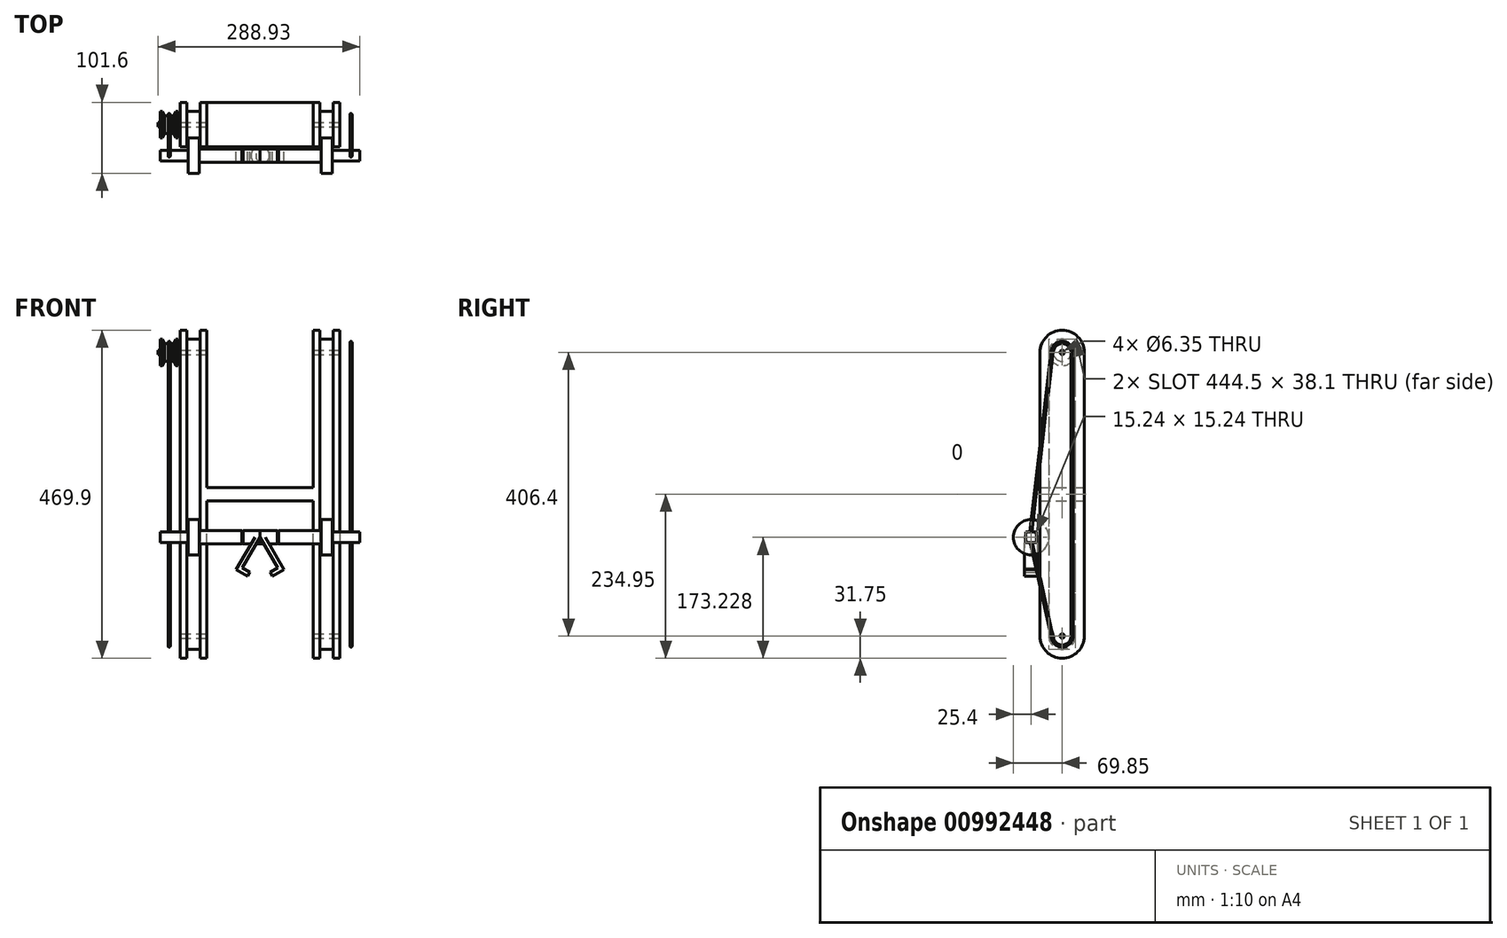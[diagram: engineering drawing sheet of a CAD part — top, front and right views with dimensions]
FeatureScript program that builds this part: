
annotation { "Feature Type Name" : "Feature", "Feature Type Description" : "" }
export const myFeature = defineFeature(function(context is Context, id is Id, definition is map)
    precondition{}
    {
        {
            var Q0;
            Q0=qCreatedBy(makeId("Front.planeOp"),FACE);
            var sketch = newSketch(context, id + "F0", { "sketchPlane" : qUnion([Q0])});
            skLineSegment(sketch, "E0", {"start": v(0, -9.53) * mm, "end": v(0, 9.53) * mm});
            skLineSegment(sketch, "E1", {"start": v(0, 9.53) * mm, "end": v(-76.2, 9.52) * mm});
            skLineSegment(sketch, "E2", {"start": v(-76.2, 9.53) * mm, "end": v(-76.2, 203.2) * mm});
            skLineSegment(sketch, "E3", {"start": v(-76.2, 203.2) * mm, "end": v(-114.3, 203.2) * mm});
            skLineSegment(sketch, "E4", {"start": v(-114.3, 203.2) * mm, "end": v(-114.3, -203.2) * mm});
            skLineSegment(sketch, "E5", {"start": v(-114.3, -203.2) * mm, "end": v(-76.2, -203.2) * mm});
            skLineSegment(sketch, "E6", {"start": v(-76.2, -203.2) * mm, "end": v(-76.2, -9.53) * mm});
            skLineSegment(sketch, "E7", {"start": v(-76.2, -9.53) * mm, "end": v(0, -9.53) * mm});
            skSolve(sketch);
        }
        {
            var Q0;
            Q0=makeQuery(id+"F0.imprint","IMPRINT",FACE,{"disambiguationData":[TD([[makeQuery(id+"F0.imprint","IMPRINT",EDGE,{"derivedFrom":sQuery(id+"F0.wireOp",EDGE,"E0")}),1.0]])]});
            extrude(context, id + "F1", {"entities" : qUnion([Q0]), "endBound" : BoundingType.SYMMETRIC, "depth" : 63.5 * mm, "offsetDistance" : 25.4 * mm});
        }
        {
            var Q0;
            Q0=makeQuery(id+"F1.opExtrude","SWEPT_FACE",FACE,{"disambiguationData":[OSD([sQuery(id+"F0.wireOp",EDGE,"E4")])]});
            var sketch = newSketch(context, id + "F2", { "sketchPlane" : qUnion([Q0])});
            skCircle(sketch, "E8", {"center": v(0, 203.2) * mm, "radius": 31.75 * mm});
            skCircle(sketch, "E9", {"center": v(0, -203.2) * mm, "radius": 31.75 * mm});
            skSolve(sketch);
        }
        {
            var Q0;
            Q0 = qSketchRegion(id + "F2", true);
            var Q1;
            Q1=makeQuery(id+"F1.opExtrude","SWEPT_FACE",FACE,{"disambiguationData":[OSD([sQuery(id+"F0.wireOp",EDGE,"E2")])]});
            extrude(context, id + "F3", {"entities" : qUnion([Q0]), "operationType" : NewBodyOperationType.ADD, "endBound" : BoundingType.UP_TO_SURFACE, "oppositeDirection" : true, "depth" : 25.4 * mm, "endBoundEntityFace" : qUnion([Q1]), "offsetDistance" : 25.4 * mm});
        }
        {
            var Q0;
            Q0=qCreatedBy(makeId("Front.planeOp"),FACE);
            var sketch = newSketch(context, id + "F4", { "sketchPlane" : qUnion([Q0])});
            skLineSegment(sketch, "E10", {"start": v(-114.3, 234.95) * mm, "end": v(-76.2, 234.95) * mm, "construction": true});
            skLineSegment(sketch, "E11.0", {"start": v(-76.2, 203.2) * mm, "end": v(-114.3, 203.2) * mm, "construction": true});
            skLineSegment(sketch, "E12.0", {"start": v(-114.3, 203.2) * mm, "end": v(-114.3, 234.95) * mm, "construction": true});
            skLineSegment(sketch, "E13.0", {"start": v(-76.2, 203.2) * mm, "end": v(-76.2, 234.95) * mm, "construction": true});
            skLineSegment(sketch, "E14", {"start": v(-114.3, 234.95) * mm, "end": v(-104.77, 234.95) * mm, "construction": true});
            skLineSegment(sketch, "E15", {"start": v(-104.77, 234.95) * mm, "end": v(-104.77, 222.25) * mm});
            skLineSegment(sketch, "E16", {"start": v(-104.77, 222.25) * mm, "end": v(-85.72, 222.25) * mm});
            skLineSegment(sketch, "E17", {"start": v(-85.72, 222.25) * mm, "end": v(-85.72, 234.95) * mm});
            skLineSegment(sketch, "E18", {"start": v(-85.72, 234.95) * mm, "end": v(-76.2, 234.95) * mm, "construction": true});
            skLineSegment(sketch, "E19", {"start": v(-104.77, 234.95) * mm, "end": v(-85.72, 234.95) * mm});
            skSolve(sketch);
        }
        {
            var Q0;
            Q0 = qSketchRegion(id + "F4", true);
            var Q1;
            Q1=makeQuery(id+"F3.opExtrude","CAP_EDGE",EDGE,{"disambiguationData":[OSD([sQuery(id+"F2.wireOp",EDGE,"E8")])],"isStart":true});
            var Q2;
            Q2=makeQuery(id+"F1.opExtrude","CAP_EDGE",EDGE,{"disambiguationData":[OSD([sQuery(id+"F0.wireOp",EDGE,"E4")])],"isStart":false});
            var Q3;
            Q3=makeQuery(id+"F1.opExtrude","CAP_EDGE",EDGE,{"disambiguationData":[OSD([sQuery(id+"F0.wireOp",EDGE,"E4")])],"isStart":true});
            var Q4;
            Q4=makeQuery(id+"F3.opExtrude","CAP_EDGE",EDGE,{"disambiguationData":[OSD([sQuery(id+"F2.wireOp",EDGE,"E9")])],"isStart":true});
            sweep(context, id + "F5", {"operationType" : NewBodyOperationType.REMOVE, "profiles" : qUnion([Q0]), "path" : qUnion([Q1, Q2, Q3, Q4])});
        }
        {
            var Q0;
            Q0=makeQuery(id+"F1.opExtrude","SWEPT_BODY",BODY,{"disambiguationData":[OSD([sQuery(id+"F0.wireOp",EDGE,"E0"),sQuery(id+"F0.wireOp",EDGE,"E1"),sQuery(id+"F0.wireOp",EDGE,"E2"),sQuery(id+"F0.wireOp",EDGE,"E3"),sQuery(id+"F0.wireOp",EDGE,"E4"),sQuery(id+"F0.wireOp",EDGE,"E5"),sQuery(id+"F0.wireOp",EDGE,"E6"),sQuery(id+"F0.wireOp",EDGE,"E7")])]});
            var Q1;
            Q1=qCreatedBy(makeId("Right.planeOp"),FACE);
            mirror(context, id + "F6", {"operationType" : NewBodyOperationType.ADD, "entities" : qUnion([Q0]), "mirrorPlane" : qUnion([Q1])});
        }
        {
            var Q0;
            Q0=makeQuery(id+"F6.opPattern","COPY",FACE,{"derivedFrom":makeQuery(id+"F3.boolean.opBoolean","MERGE",FACE,{"derivedFrom":[makeQuery(id+"F1.opExtrude","SWEPT_FACE",FACE,{"disambiguationData":[OSD([sQuery(id+"F0.wireOp",EDGE,"E4")])]}),makeQuery(id+"F3.opExtrude","CAP_FACE",FACE,{"disambiguationData":[OSD([sQuery(id+"F2.wireOp",EDGE,"E8")])],"isStart":true}),makeQuery(id+"F3.opExtrude","CAP_FACE",FACE,{"disambiguationData":[OSD([sQuery(id+"F2.wireOp",EDGE,"E9")])],"isStart":true})]}),"instanceName":"1"});
            var sketch = newSketch(context, id + "F7", { "sketchPlane" : qUnion([Q0])});
            skArc(sketch, "E20.0", {"start": v(-31.75, 203.2) * mm, "mid": v(0, 234.95) * mm, "end": v(31.75, 203.2) * mm, "construction": true});
            skCircle(sketch, "E21", {"center": v(0, 203.2) * mm, "radius": 3.18 * mm});
            skCircle(sketch, "E22.MirrorC", {"center": v(0, -203.2) * mm, "radius": 3.18 * mm});
            skSolve(sketch);
        }
        {
            var Q0;
            Q0 = qSketchRegion(id + "F7", true);
            extrude(context, id + "F8", {"entities" : qUnion([Q0]), "operationType" : NewBodyOperationType.REMOVE, "endBound" : BoundingType.THROUGH_ALL, "oppositeDirection" : true, "depth" : 25.4 * mm, "offsetDistance" : 25.4 * mm});
        }
        {
            var Q0;
            Q0=qCreatedBy(makeId("Front.planeOp"),FACE);
            var sketch = newSketch(context, id + "F9", { "sketchPlane" : qUnion([Q0])});
            skLineSegment(sketch, "E23.0", {"start": v(-104.77, 203.2) * mm, "end": v(-114.3, 203.2) * mm});
            skLineSegment(sketch, "E24.0", {"start": v(-114.3, 203.2) * mm, "end": v(-114.3, 234.95) * mm, "construction": true});
            skLineSegment(sketch, "E25", {"start": v(-114.3, 203.2) * mm, "end": v(-146.05, 203.2) * mm});
            skLineSegment(sketch, "E26", {"start": v(-146.05, 203.2) * mm, "end": v(-146.05, 206.38) * mm});
            skLineSegment(sketch, "E27", {"start": v(-146.05, 206.38) * mm, "end": v(-142.87, 206.38) * mm});
            skLineSegment(sketch, "E28", {"start": v(-142.87, 206.38) * mm, "end": v(-142.87, 222.25) * mm});
            skLineSegment(sketch, "E29", {"start": v(-142.87, 222.25) * mm, "end": v(-139.7, 222.25) * mm});
            skLineSegment(sketch, "E30", {"start": v(-139.7, 222.25) * mm, "end": v(-136.52, 215.9) * mm});
            skLineSegment(sketch, "E31", {"start": v(-136.52, 215.9) * mm, "end": v(-123.82, 215.9) * mm});
            skLineSegment(sketch, "E32", {"start": v(-123.82, 215.9) * mm, "end": v(-120.65, 222.25) * mm});
            skLineSegment(sketch, "E33", {"start": v(-120.65, 222.25) * mm, "end": v(-117.47, 222.25) * mm});
            skLineSegment(sketch, "E34", {"start": v(-117.47, 222.25) * mm, "end": v(-117.47, 206.38) * mm});
            skLineSegment(sketch, "E35", {"start": v(-117.47, 206.38) * mm, "end": v(-114.3, 206.38) * mm});
            skLineSegment(sketch, "E36", {"start": v(-114.3, 206.38) * mm, "end": v(-114.3, 203.2) * mm});
            skCircle(sketch, "E37", {"center": v(-130.17, 217.49) * mm, "radius": 1.59 * mm});
            skPoint(sketch, "E38", {"position": v(-130.17, 215.9) * mm});
            skSolve(sketch);
        }
        {
            var Q0;
            Q0=makeQuery(id+"F9.imprint","IMPRINT",FACE,{"disambiguationData":[TD([[makeQuery(id+"F9.imprint","IMPRINT",EDGE,{"derivedFrom":sQuery(id+"F9.wireOp",EDGE,"E25")}),-1.0]])]});
            var Q1;
            Q1=sQuery(id+"F9.wireOp",EDGE,"E25");
            revolve(context, id + "F10", {"surfaceOperationType" : NewSurfaceOperationType.NEW, "entities" : qUnion([Q0]), "axis" : qUnion([Q1]), "revolveType" : RevolveType.FULL});
        }
        {
            var Q0;
            Q0=qCreatedBy(makeId("Top.planeOp"),FACE);
            var sketch = newSketch(context, id + "F11", { "sketchPlane" : qUnion([Q0])});
            skLineSegment(sketch, "E39.0", {"start": v(-104.77, -19.05) * mm, "end": v(-85.72, -19.05) * mm, "construction": true});
            skLineSegment(sketch, "E40.0", {"start": v(76.2, -31.75) * mm, "end": v(-76.2, -31.75) * mm, "construction": true});
            skLineSegment(sketch, "E41", {"start": v(-103.19, -44.45) * mm, "end": v(-103.19, -19.05) * mm});
            skLineSegment(sketch, "E42", {"start": v(-103.19, -19.05) * mm, "end": v(-87.31, -19.05) * mm});
            skLineSegment(sketch, "E43", {"start": v(-87.31, -19.05) * mm, "end": v(-87.31, -34.93) * mm});
            skLineSegment(sketch, "E44", {"start": v(-87.31, -34.93) * mm, "end": v(0, -34.92) * mm, "construction": true});
            skLineSegment(sketch, "E45", {"start": v(0, -34.92) * mm, "end": v(0, -44.45) * mm});
            skLineSegment(sketch, "E46", {"start": v(0, -44.45) * mm, "end": v(-103.19, -44.45) * mm});
            skLineSegment(sketch, "E47", {"start": v(-87.31, -34.93) * mm, "end": v(-26.32, -34.92) * mm});
            skLineSegment(sketch, "E48", {"start": v(-26.32, -34.92) * mm, "end": v(-25.4, -36.51) * mm});
            skLineSegment(sketch, "E49", {"start": v(-25.4, -36.51) * mm, "end": v(-24.48, -34.92) * mm});
            skLineSegment(sketch, "E50", {"start": v(-24.48, -34.92) * mm, "end": v(0, -34.92) * mm});
            skSolve(sketch);
        }
        {
            var Q0;
            Q0=makeQuery(id+"F11.imprint","IMPRINT",FACE,{"disambiguationData":[TD([[makeQuery(id+"F11.imprint","IMPRINT",EDGE,{"derivedFrom":sQuery(id+"F11.wireOp",EDGE,"E41")}),-1.0]])]});
            var Q1;
            Q1=sQuery(id+"F11.wireOp",EDGE,"E46");
            revolve(context, id + "F12", {"surfaceOperationType" : NewSurfaceOperationType.NEW, "entities" : qUnion([Q0]), "axis" : qUnion([Q1]), "revolveType" : RevolveType.FULL});
        }
        {
            var Q0;
            Q0=qCreatedBy(makeId("Front.planeOp"),FACE);
            var Q1;
            Q1=sQuery(id+"F11.wireOp",VERTEX,"E45.end");
            cPlane(context, id + "F13", {"entities" : qUnion([Q0, Q1]), "cplaneType" : CPlaneType.PLANE_POINT, "offset" : 25.4 * mm, "width" : 152.4 * mm, "height" : 152.4 * mm});
        }
        {
            var Q0;
            Q0=qCreatedBy(id+"F13.planeOp",FACE);
            var sketch = newSketch(context, id + "F14", { "sketchPlane" : qUnion([Q0])});
            skLineSegment(sketch, "E51", {"start": v(0, 0) * mm, "end": v(-25.4, -44) * mm});
            skLineSegment(sketch, "E52", {"start": v(-25.4, -44) * mm, "end": v(-14.4, -50.34) * mm});
            skLineSegment(sketch, "E53", {"start": v(-14.4, -50.34) * mm, "end": v(-17.58, -55.84) * mm});
            skLineSegment(sketch, "E54", {"start": v(-17.58, -55.84) * mm, "end": v(-34.07, -46.32) * mm});
            skLineSegment(sketch, "E55", {"start": v(-34.07, -46.32) * mm, "end": v(-7.33, 0) * mm});
            skLineSegment(sketch, "E56", {"start": v(-7.33, 0) * mm, "end": v(0, 0) * mm});
            skLineSegment(sketch, "E57", {"start": v(-25.4, -44) * mm, "end": v(-30.9, -40.82) * mm, "construction": true});
            skSolve(sketch);
        }
        {
            var Q0;
            Q0 = qSketchRegion(id + "F14", true);
            extrude(context, id + "F15", {"entities" : qUnion([Q0]), "operationType" : NewBodyOperationType.ADD, "endBound" : BoundingType.SYMMETRIC, "depth" : 19.05 * mm, "offsetDistance" : 25.4 * mm});
        }
        {
            var Q0;
            Q0=makeQuery(id+"F12.opRevolve","SWEPT_BODY",BODY,{"disambiguationData":[OSD([sQuery(id+"F11.wireOp",EDGE,"E41"),sQuery(id+"F11.wireOp",EDGE,"E42"),sQuery(id+"F11.wireOp",EDGE,"E43"),sQuery(id+"F11.wireOp",EDGE,"E45"),sQuery(id+"F11.wireOp",EDGE,"E46"),sQuery(id+"F11.wireOp",EDGE,"E47"),sQuery(id+"F11.wireOp",EDGE,"E48"),sQuery(id+"F11.wireOp",EDGE,"E49"),sQuery(id+"F11.wireOp",EDGE,"E50")])]});
            transform(context, id + "F16", {"entities" : qUnion([Q0]), "transformType" : TransformType.TRANSLATION_3D, "dx" : 0 * mm, "dy" : 0 * mm, "dz" : -61.72 * mm, "makeCopy" : false});
        }
        {
            var Q0;
            Q0=qCreatedBy(makeId("Right.planeOp"),FACE);
            var sketch = newSketch(context, id + "F17", { "sketchPlane" : qUnion([Q0])});
            skCircle(sketch, "E58.0", {"center": v(0, 203.2) * mm, "radius": 12.7 * mm, "construction": true});
            skCircle(sketch, "E59.0.0", {"center": v(-44.45, -61.72) * mm, "radius": 25.4 * mm, "construction": true});
            skCircle(sketch, "E60.MirrorC", {"center": v(0, -203.2) * mm, "radius": 12.7 * mm, "construction": true});
            skLineSegment(sketch, "E61", {"start": v(-12.61, 204.7) * mm, "end": v(-44.45, -61.72) * mm});
            skLineSegment(sketch, "E62", {"start": v(-44.45, -61.72) * mm, "end": v(-12.4, -205.96) * mm});
            skLineSegment(sketch, "E63", {"start": v(12.7, -203.2) * mm, "end": v(12.7, 203.2) * mm});
            skArc(sketch, "E64", {"start": v(12.7, 203.2) * mm, "mid": v(0.75, 215.88) * mm, "end": v(-12.61, 204.7) * mm});
            skArc(sketch, "E65", {"start": v(-12.4, -205.96) * mm, "mid": v(1.39, -215.82) * mm, "end": v(12.7, -203.2) * mm});
            skSolve(sketch);
        }
        {
            var Q0;
            Q0=makeQuery(id+"F9.imprint","IMPRINT",FACE,{"disambiguationData":[TD([[makeQuery(id+"F9.imprint","IMPRINT",EDGE,{"derivedFrom":sQuery(id+"F9.wireOp",EDGE,"E37")}),1.0]])]});
            var Q1;
            Q1 = qConstructionFilter(qBodyType(qCreatedBy(id + "F17" ,EDGE), BodyType.WIRE), ConstructionObject.NO);
            sweep(context, id + "F18", {"profiles" : qUnion([Q0]), "path" : qUnion([Q1])});
        }
        {
            var Q0;
            Q0=makeQuery(id+"F12.opRevolve","SWEPT_FACE",FACE,{"disambiguationData":[OSD([sQuery(id+"F11.wireOp",EDGE,"E41")])]});
            var sketch = newSketch(context, id + "F19", { "sketchPlane" : qUnion([Q0])});
            skCircle(sketch, "E66.0", {"center": v(44.45, -61.72) * mm, "radius": 25.4 * mm, "construction": true});
            skLineSegment(sketch, "E67.bottom", {"start": v(52.07, -54.1) * mm, "end": v(36.83, -54.1) * mm});
            skLineSegment(sketch, "E67.top", {"start": v(52.07, -69.34) * mm, "end": v(36.83, -69.34) * mm});
            skLineSegment(sketch, "E67.left", {"start": v(52.07, -54.1) * mm, "end": v(52.07, -69.34) * mm});
            skLineSegment(sketch, "E67.right", {"start": v(36.83, -54.1) * mm, "end": v(36.83, -69.34) * mm});
            skSolve(sketch);
        }
        {
            var Q0;
            Q0=makeQuery(id+"F19.imprint","IMPRINT",FACE,{"disambiguationData":[TD([[makeQuery(id+"F19.imprint","IMPRINT",EDGE,{"derivedFrom":sQuery(id+"F19.wireOp",EDGE,"E67.bottom")}),1.0]])]});
            var Q1;
            Q1=makeQuery(id+"F10.opRevolve","SWEPT_FACE",FACE,{"disambiguationData":[OSD([sQuery(id+"F9.wireOp",EDGE,"E28")])]});
            extrude(context, id + "F20", {"entities" : qUnion([Q0]), "operationType" : NewBodyOperationType.ADD, "endBound" : BoundingType.UP_TO_SURFACE, "depth" : 25.4 * mm, "endBoundEntityFace" : qUnion([Q1]), "offsetDistance" : 25.4 * mm});
        }
        {
            var Q0;
            Q0=makeQuery(id+"F12.opRevolve","SWEPT_BODY",BODY,{"disambiguationData":[OSD([sQuery(id+"F11.wireOp",EDGE,"E41"),sQuery(id+"F11.wireOp",EDGE,"E42"),sQuery(id+"F11.wireOp",EDGE,"E43"),sQuery(id+"F11.wireOp",EDGE,"E45"),sQuery(id+"F11.wireOp",EDGE,"E46"),sQuery(id+"F11.wireOp",EDGE,"E47"),sQuery(id+"F11.wireOp",EDGE,"E48"),sQuery(id+"F11.wireOp",EDGE,"E49"),sQuery(id+"F11.wireOp",EDGE,"E50")])]});
            var Q1;
            Q1=qCreatedBy(makeId("Right.planeOp"),FACE);
            mirror(context, id + "F21", {"operationType" : NewBodyOperationType.ADD, "entities" : qUnion([Q0]), "mirrorPlane" : qUnion([Q1])});
        }
    });
